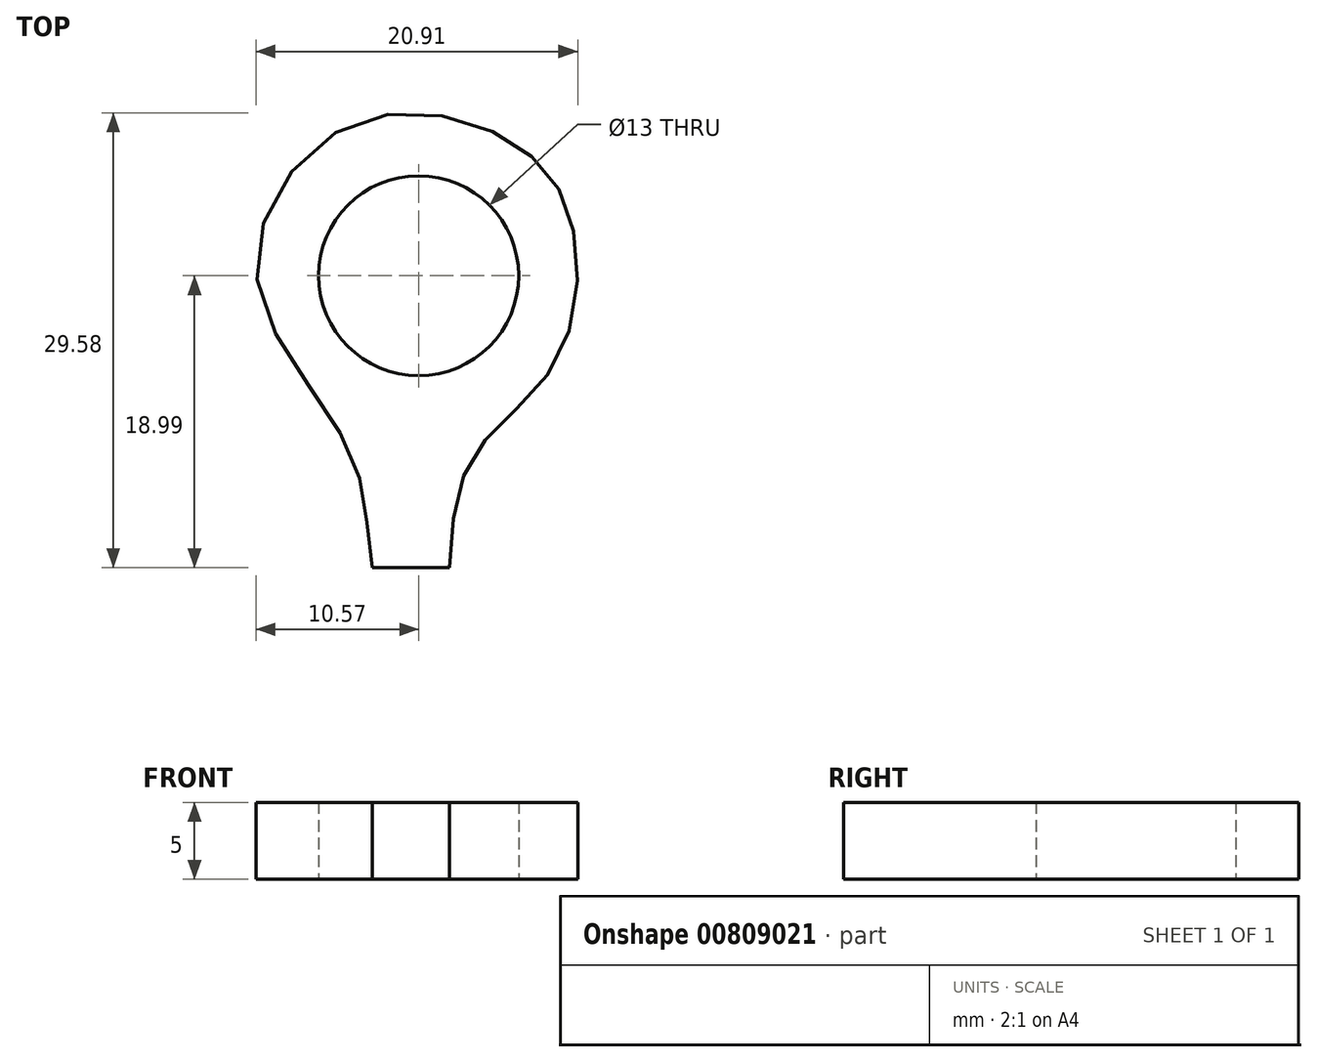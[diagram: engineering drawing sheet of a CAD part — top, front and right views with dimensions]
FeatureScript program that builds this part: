
annotation { "Feature Type Name" : "Feature", "Feature Type Description" : "" }
export const myFeature = defineFeature(function(context is Context, id is Id, definition is map)
    precondition{}
    {
        {
            var Q0;
            Q0=qCreatedBy(makeId("Top.planeOp"),FACE);
            var sketch = newSketch(context, id + "F0", { "sketchPlane" : qUnion([Q0])});
            skCircle(sketch, "E0", {"center": v(0, 0) * mm, "radius": 6.5 * mm});
            skFitSpline(sketch, "E1", {"points": [v(-3.02, -19) * mm, v(-4.58, -11.16) * mm, v(-10.53, 0) * mm, v(-4.43, 9.81) * mm, v(5.75, 8.87) * mm, v(9.97, 3.4) * mm, v(8.88, -5.68) * mm, v(3.71, -11.48) * mm, v(1.99, -19) * mm], "startDerivative": vector(-11.26, 69.55) * mm, "endDerivative": vector(-3.6, -77.5) * mm});
            skLineSegment(sketch, "E2", {"start": v(-3.02, -19) * mm, "end": v(1.99, -19) * mm});
            skSolve(sketch);
        }
        {
            var Q0;
            Q0=makeQuery(id+"F0.imprint","IMPRINT",FACE,{"disambiguationData":[TD([[makeQuery(id+"F0.imprint","IMPRINT",EDGE,{"derivedFrom":sQuery(id+"F0.wireOp",EDGE,"E0")}),-1.0]])]});
            extrude(context, id + "F1", {"entities" : qUnion([Q0]), "depth" : 5 * mm, "offsetDistance" : 25 * mm});
        }
    });
